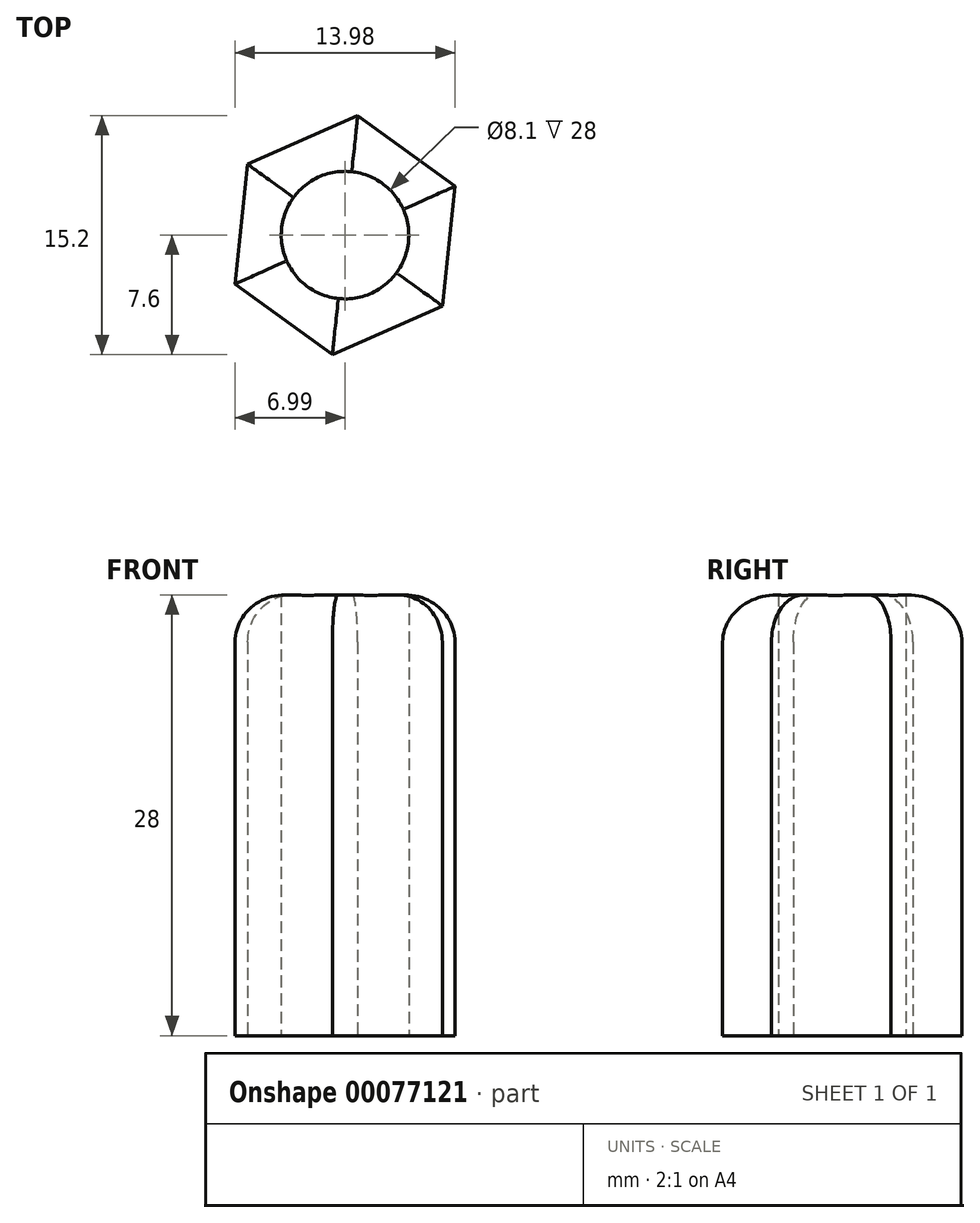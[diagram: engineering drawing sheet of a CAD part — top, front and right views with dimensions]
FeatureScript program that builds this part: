
annotation { "Feature Type Name" : "Feature", "Feature Type Description" : "" }
export const myFeature = defineFeature(function(context is Context, id is Id, definition is map)
    precondition{}
    {
        {
            var Q0;
            Q0=qCreatedBy(makeId("Top.planeOp"),FACE);
            var sketch = newSketch(context, id + "F0", { "sketchPlane" : qUnion([Q0])});
            skCircle(sketch, "E0", {"center": v(0, 0) * mm, "radius": 4.05 * mm});
            skCircle(sketch, "E1.cCircle", {"center": v(0, 0) * mm, "radius": 7.64 * mm, "construction": true});
            skLineSegment(sketch, "E1.0", {"start": v(6.99, 3.1) * mm, "end": v(6.18, -4.5) * mm});
            skLineSegment(sketch, "E1.1", {"start": v(6.18, -4.5) * mm, "end": v(-0.8, -7.6) * mm});
            skLineSegment(sketch, "E1.2", {"start": v(-0.8, -7.6) * mm, "end": v(-6.99, -3.1) * mm});
            skLineSegment(sketch, "E1.3", {"start": v(-6.99, -3.1) * mm, "end": v(-6.18, 4.5) * mm});
            skLineSegment(sketch, "E1.4", {"start": v(-6.18, 4.5) * mm, "end": v(0.8, 7.6) * mm});
            skLineSegment(sketch, "E1.5", {"start": v(0.8, 7.6) * mm, "end": v(6.99, 3.1) * mm});
            skSolve(sketch);
        }
        {
            var Q0;
            Q0=makeQuery(id+"F0.imprint","IMPRINT",FACE,{"disambiguationData":[TD([[makeQuery(id+"F0.imprint","IMPRINT",EDGE,{"derivedFrom":sQuery(id+"F0.wireOp",EDGE,"E0")}),-1.0]])]});
            extrude(context, id + "F1", {"entities" : qUnion([Q0]), "depth" : 28 * mm});
        }
        {
            var Q0;
            Q0=makeQuery(id+"F1.opExtrude","CAP_EDGE",EDGE,{"disambiguationData":[OSD([sQuery(id+"F0.wireOp",EDGE,"E1.1")])],"isStart":false});
            var Q1;
            Q1=makeQuery(id+"F1.opExtrude","CAP_EDGE",EDGE,{"disambiguationData":[OSD([sQuery(id+"F0.wireOp",EDGE,"E1.2")])],"isStart":false});
            var Q2;
            Q2=makeQuery(id+"F1.opExtrude","CAP_EDGE",EDGE,{"disambiguationData":[OSD([sQuery(id+"F0.wireOp",EDGE,"E1.3")])],"isStart":false});
            var Q3;
            Q3=makeQuery(id+"F1.opExtrude","CAP_EDGE",EDGE,{"disambiguationData":[OSD([sQuery(id+"F0.wireOp",EDGE,"E1.4")])],"isStart":false});
            var Q4;
            Q4=makeQuery(id+"F1.opExtrude","CAP_EDGE",EDGE,{"disambiguationData":[OSD([sQuery(id+"F0.wireOp",EDGE,"E1.5")])],"isStart":false});
            var Q5;
            Q5=makeQuery(id+"F1.opExtrude","CAP_EDGE",EDGE,{"disambiguationData":[OSD([sQuery(id+"F0.wireOp",EDGE,"E1.0")])],"isStart":false});
            fillet(context, id + "F2", {"entities" : qUnion([Q0, Q1, Q2, Q3, Q4, Q5]), "radius" : 3 * mm, "tangentPropagation" : true, "allowEdgeOverflow" : false});
        }
    });
